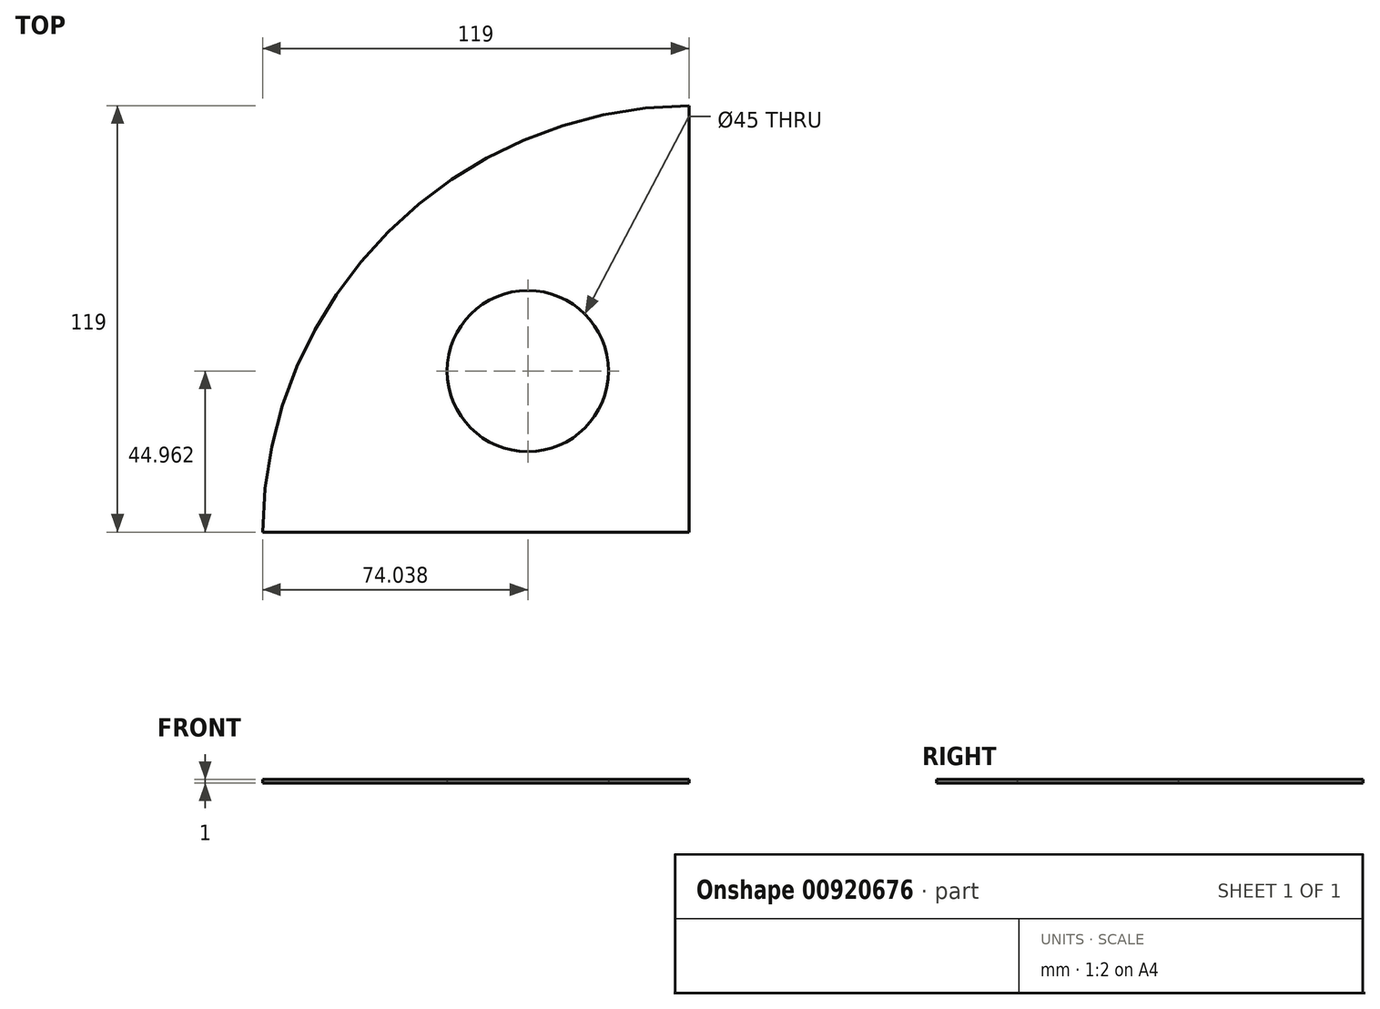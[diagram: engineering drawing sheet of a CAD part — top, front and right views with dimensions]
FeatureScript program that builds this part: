
annotation { "Feature Type Name" : "Feature", "Feature Type Description" : "" }
export const myFeature = defineFeature(function(context is Context, id is Id, definition is map)
    precondition{}
    {
        {
            var Q0;
            Q0=qCreatedBy(makeId("Top.planeOp"),FACE);
            var sketch = newSketch(context, id + "F0", { "sketchPlane" : qUnion([Q0])});
            skCircle(sketch, "E0", {"center": v(0, 0) * mm, "radius": 120 * mm});
            skCircle(sketch, "E1", {"center": v(0, 0) * mm, "radius": 65 * mm, "construction": true});
            skLineSegment(sketch, "E2", {"start": v(0, 0) * mm, "end": v(-107.78, 107.78) * mm, "construction": true});
            skCircle(sketch, "E3", {"center": v(-45.96, 45.96) * mm, "radius": 22.5 * mm});
            skLineSegment(sketch, "E4", {"start": v(0, 0) * mm, "end": v(-120, 0) * mm, "construction": true});
            skLineSegment(sketch, "E5", {"start": v(0, 0) * mm, "end": v(0, 120) * mm, "construction": true});
            skLineSegment(sketch, "E6.0", {"start": v(-1, 1) * mm, "end": v(-120, 1) * mm});
            skLineSegment(sketch, "E6.1", {"start": v(-1, 1) * mm, "end": v(-1, 120) * mm});
            skSolve(sketch);
        }
        {
            var Q0;
            Q0=makeQuery(id+"F0.imprint","IMPRINT",FACE,{"disambiguationData":[TD([[makeQuery(id+"F0.imprint","IMPRINT",EDGE,{"derivedFrom":sQuery(id+"F0.wireOp",EDGE,"E3")}),-1.0]])]});
            extrude(context, id + "F1", {"entities" : qUnion([Q0]), "depth" : 1 * mm, "offsetDistance" : 25 * mm});
        }
    });
